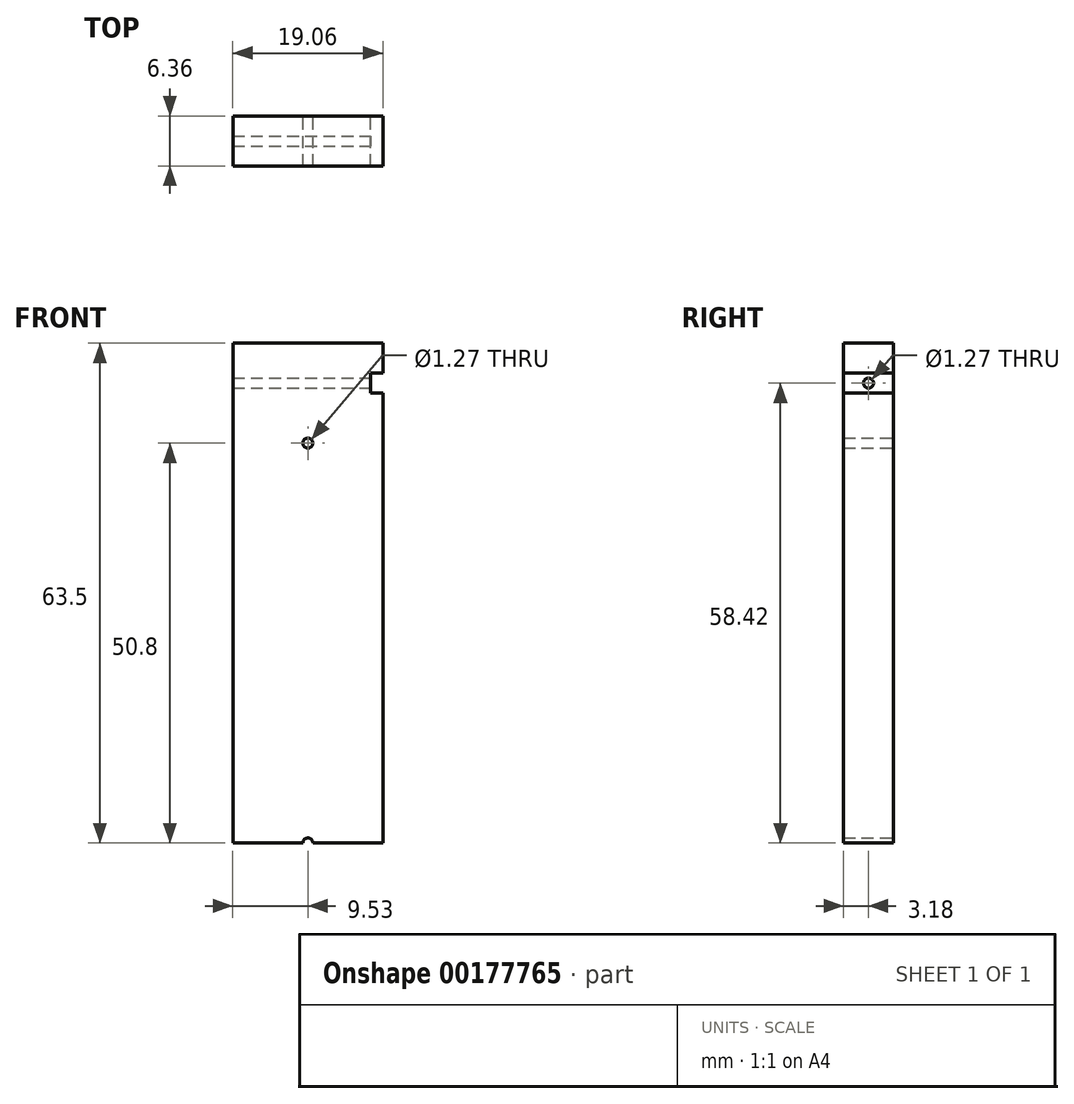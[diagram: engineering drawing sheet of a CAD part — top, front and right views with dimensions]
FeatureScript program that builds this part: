
annotation { "Feature Type Name" : "Feature", "Feature Type Description" : "" }
export const myFeature = defineFeature(function(context is Context, id is Id, definition is map)
    precondition{}
    {
        {
            var Q0;
            Q0=qCreatedBy(makeId("Front.planeOp"),FACE);
            var sketch = newSketch(context, id + "F0", { "sketchPlane" : qUnion([Q0])});
            skLineSegment(sketch, "E0.bottom", {"start": v(9.53, 63.5) * mm, "end": v(-9.53, 63.5) * mm});
            skLineSegment(sketch, "E0.top", {"start": v(9.52, 0) * mm, "end": v(-9.52, 0) * mm});
            skLineSegment(sketch, "E0.left", {"start": v(9.52, 63.5) * mm, "end": v(9.52, 0) * mm});
            skLineSegment(sketch, "E0.right", {"start": v(-9.53, 63.5) * mm, "end": v(-9.53, 0) * mm});
            skPoint(sketch, "E0.middle", {"position": v(0, 31.75) * mm});
            skArc(sketch, "E1", {"start": v(9.52, 0) * mm, "mid": v(7.86, -5.38) * mm, "end": v(3.45, -8.88) * mm});
            skArc(sketch, "E2.trimOffspring", {"start": v(0, -9.52) * mm, "mid": v(-6.74, -6.74) * mm, "end": v(-9.52, 0) * mm});
            skCircle(sketch, "E3", {"center": v(0, 0) * mm, "radius": 0.64 * mm});
            skLineSegment(sketch, "E4", {"start": v(0, 63.5) * mm, "end": v(0, 50.8) * mm});
            skPoint(sketch, "E4.endSnap0", {"position": v(0, 63.5) * mm});
            skCircle(sketch, "E5", {"center": v(0, 50.8) * mm, "radius": 0.64 * mm});
            skLineSegment(sketch, "E6", {"start": v(9.52, 63.5) * mm, "end": v(9.52, 58.42) * mm});
            skLineSegment(sketch, "E7.bottom", {"start": v(9.52, 59.69) * mm, "end": v(7.98, 59.69) * mm});
            skLineSegment(sketch, "E7.top", {"start": v(9.52, 57.15) * mm, "end": v(7.98, 57.15) * mm});
            skLineSegment(sketch, "E7.left", {"start": v(9.52, 59.69) * mm, "end": v(9.52, 57.15) * mm});
            skLineSegment(sketch, "E7.right", {"start": v(7.98, 59.69) * mm, "end": v(7.98, 57.15) * mm});
            skLineSegment(sketch, "E8", {"start": v(0, -9.52) * mm, "end": v(1.38, -5.55) * mm});
            skLineSegment(sketch, "E9", {"start": v(1.38, -5.55) * mm, "end": v(0, 0) * mm});
            skLineSegment(sketch, "E10", {"start": v(1.38, -5.55) * mm, "end": v(3.45, -8.88) * mm});
            skSolve(sketch);
        }
        {
            var Q0;
            {var subQ4=sQuery(id+"F0.wireOp",EDGE,"E0.left");Q0=makeQuery(id+"F0.imprint","IMPRINT",FACE,{"disambiguationData":[TD([[makeQuery(id+"F0.imprint","IMPRINT",EDGE,{"derivedFrom":subQ4}),-1.0]])]});}
            var Q1;
            {var subQ0=sQuery(id+"F0.wireOp",EDGE,"E1");Q1=makeQuery(id+"F0.imprint","IMPRINT",FACE,{"disambiguationData":[TD([[makeQuery(id+"F0.imprint","IMPRINT",EDGE,{"derivedFrom":subQ0}),-1.0]])]});}
            var Q2;
            Q2=makeQuery(id+"F0.imprint","IMPRINT",FACE,{"disambiguationData":[TD([[makeQuery(id+"F0.imprint","IMPRINT",EDGE,{"derivedFrom":sQuery(id+"F0.wireOp",EDGE,"IJkfLoIr-6Cm8-4THf-EOu6-uUzx7VYciygS.bottom")}),1.0]])]});
            var Q3;
            Q3=makeQuery(id+"F0.imprint","IMPRINT",FACE,{"disambiguationData":[TD([[makeQuery(id+"F0.imprint","IMPRINT",EDGE,{"derivedFrom":sQuery(id+"F0.wireOp",EDGE,"IJkfLoIr-6Cm8-4THf-EOu6-uUzx7VYciygS.bottom")}),-1.0]])]});
            var Q4;
            {var subQ0=sQuery(id+"F0.wireOp",EDGE,"IKmFjhG5-D3xq-hnov-2SvM-noyRAvmDeqq6");Q4=makeQuery(id+"F0.imprint","IMPRINT",FACE,{"disambiguationData":[TD([[makeQuery(id+"F0.imprint","IMPRINT",EDGE,{"derivedFrom":subQ0}),1.0]])]});}
            var Q5;
            {var subQ5=sQuery(id+"F0.wireOp",EDGE,"E2.trimOffspring");Q5=makeQuery(id+"F0.imprint","IMPRINT",FACE,{"disambiguationData":[TD([[makeQuery(id+"F0.imprint","IMPRINT",EDGE,{"derivedFrom":subQ5}),-1.0]])]});}
            extrude(context, id + "F1", {"entities" : qUnion([Q0, Q1, Q2, Q3, Q4, Q5]), "endBound" : BoundingType.SYMMETRIC, "depth" : 6.35 * mm});
        }
        {
            var Q0;
            Q0=makeQuery(id+"F1.opExtrude","SWEPT_FACE",FACE,{"disambiguationData":[OSD([sQuery(id+"F0.wireOp",EDGE,"E0.left")])]});
            var sketch = newSketch(context, id + "F2", { "sketchPlane" : qUnion([Q0])});
            skLineSegment(sketch, "E11", {"start": v(0, 63.5) * mm, "end": v(0, 58.42) * mm});
            skPoint(sketch, "E11.endSnap0", {"position": v(0, 63.5) * mm});
            skCircle(sketch, "E12", {"center": v(0, 58.42) * mm, "radius": 0.64 * mm});
            skSolve(sketch);
        }
        {
            var Q0;
            Q0=sQuery(id+"F2.wireOp",VERTEX,"E12.center");
            var Q1;
            Q1=makeQuery(id+"F1.opExtrude","SWEPT_BODY",BODY,{"disambiguationData":[OSD([sQuery(id+"F0.wireOp",EDGE,"E0.bottom"),sQuery(id+"F0.wireOp",EDGE,"E0.left"),sQuery(id+"F0.wireOp",EDGE,"E0.right"),sQuery(id+"F0.wireOp",EDGE,"E1"),sQuery(id+"F0.wireOp",EDGE,"uJJD5cNK-mesi-jekV-IMYk-puXTxzckVE3S"),sQuery(id+"F0.wireOp",EDGE,"E2.trimOffspring"),sQuery(id+"F0.wireOp",EDGE,"E3")])]});
            hole(context, id + "F3", {"style" : HoleStyle.SIMPLE, "endStyle" : HoleEndStyle.THROUGH, "holeDiameter" : 1.27 * mm, "locations" : qUnion([Q0]), "scope" : qUnion([Q1]), "isTappedThrough" : true});
        }
    });
